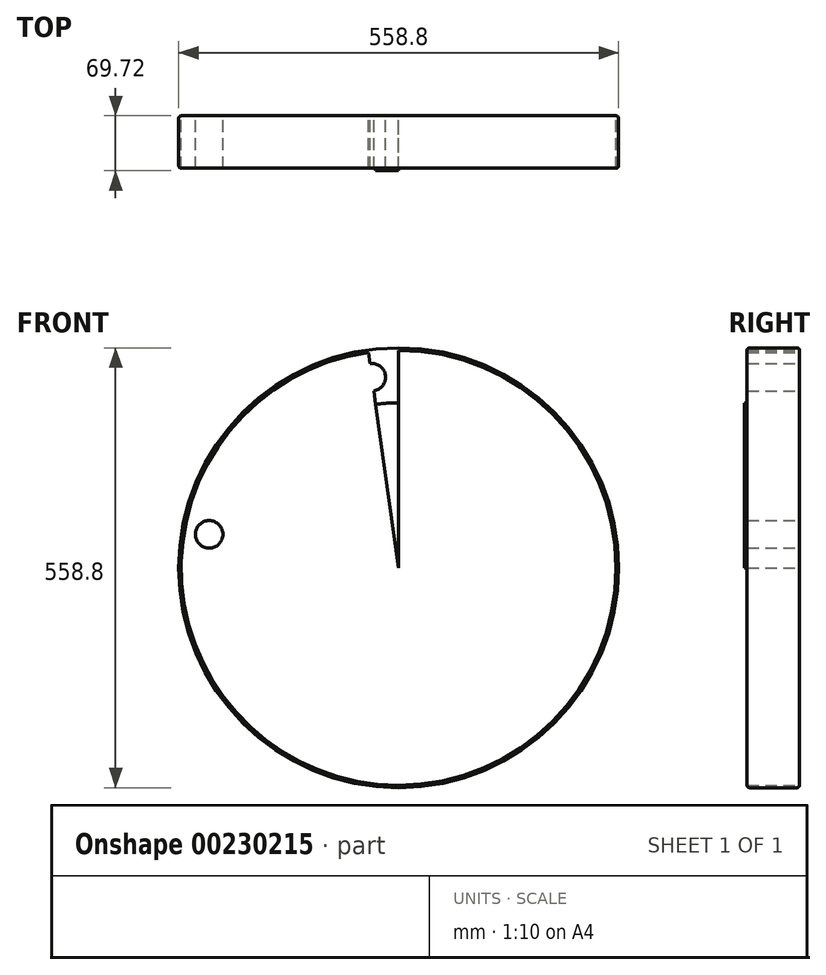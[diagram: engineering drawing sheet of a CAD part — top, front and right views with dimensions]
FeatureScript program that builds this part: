
annotation { "Feature Type Name" : "Feature", "Feature Type Description" : "" }
export const myFeature = defineFeature(function(context is Context, id is Id, definition is map)
    precondition{}
    {
        {
            var Q0;
            Q0=qCreatedBy(makeId("Front.planeOp"),FACE);
            var sketch = newSketch(context, id + "F0", { "sketchPlane" : qUnion([Q0])});
            skCircle(sketch, "E0", {"center": v(0, 0) * mm, "radius": 279.4 * mm});
            skSolve(sketch);
        }
        {
            var Q0;
            Q0 = qSketchRegion(id + "F0", true);
            extrude(context, id + "F1", {"entities" : qUnion([Q0]), "depth" : 66.55 * mm});
        }
        {
            var Q0;
            Q0=makeQuery(id+"F1.opExtrude","CAP_EDGE",EDGE,{"disambiguationData":[OSD([sQuery(id+"F0.wireOp",EDGE,"E0")])],"isStart":false});
            var Q1;
            Q1=makeQuery(id+"F1.opExtrude","CAP_EDGE",EDGE,{"disambiguationData":[OSD([sQuery(id+"F0.wireOp",EDGE,"E0")])],"isStart":true});
            fillet(context, id + "F2", {"entities" : qUnion([Q0, Q1]), "radius" : 3.17 * mm, "tangentPropagation" : true, "allowEdgeOverflow" : false});
        }
        {
            var Q0;
            Q0=makeQuery(id+"F1.opExtrude","CAP_FACE",FACE,{"disambiguationData":[OSD([sQuery(id+"F0.wireOp",EDGE,"E0")])],"isStart":false});
            var sketch = newSketch(context, id + "F3", { "sketchPlane" : qUnion([Q0])});
            skCircle(sketch, "E1", {"center": v(0, 0) * mm, "radius": 209.55 * mm});
            skSolve(sketch);
        }
        {
            var Q0;
            Q0 = qSketchRegion(id + "F3", true);
            extrude(context, id + "F4", {"entities" : qUnion([Q0]), "operationType" : NewBodyOperationType.ADD, "depth" : 3.17 * mm});
        }
        {
            var Q0;
            Q0=makeQuery(id+"F1.opExtrude","CAP_FACE",FACE,{"disambiguationData":[OSD([sQuery(id+"F0.wireOp",EDGE,"E0")])],"isStart":true});
            var sketch = newSketch(context, id + "F5", { "sketchPlane" : qUnion([Q0])});
            skCircle(sketch, "E2", {"center": v(0, 0) * mm, "radius": 244.48 * mm});
            skLineSegment(sketch, "E3", {"start": v(0, 0) * mm, "end": v(0, 323.68) * mm});
            skLineSegment(sketch, "E4", {"start": v(0, 0) * mm, "end": v(45.3, 322.28) * mm});
            skCircle(sketch, "E5", {"center": v(34.02, 242.1) * mm, "radius": 17.46 * mm});
            skCircle(sketch, "E6.1.0", {"center": v(-42.45, 240.76) * mm, "radius": 17.46 * mm});
            skCircle(sketch, "E6.2.0", {"center": v(-114.77, 215.86) * mm, "radius": 17.46 * mm});
            skCircle(sketch, "E6.3.0", {"center": v(-175.86, 169.83) * mm, "radius": 17.46 * mm});
            skCircle(sketch, "E6.4.0", {"center": v(-219.73, 107.17) * mm, "radius": 17.46 * mm});
            skCircle(sketch, "E6.5.0", {"center": v(-242.1, 34.02) * mm, "radius": 17.46 * mm});
            skCircle(sketch, "E6.6.0", {"center": v(-240.76, -42.45) * mm, "radius": 17.46 * mm});
            skCircle(sketch, "E6.7.0", {"center": v(-215.86, -114.77) * mm, "radius": 17.46 * mm});
            skCircle(sketch, "E6.8.0", {"center": v(-169.83, -175.86) * mm, "radius": 17.46 * mm});
            skCircle(sketch, "E6.9.0", {"center": v(-107.17, -219.73) * mm, "radius": 17.46 * mm});
            skCircle(sketch, "E6.10.0", {"center": v(-34.02, -242.1) * mm, "radius": 17.46 * mm});
            skCircle(sketch, "E6.11.0", {"center": v(42.45, -240.76) * mm, "radius": 17.46 * mm});
            skCircle(sketch, "E6.12.0", {"center": v(114.77, -215.86) * mm, "radius": 17.46 * mm});
            skCircle(sketch, "E6.13.0", {"center": v(175.86, -169.83) * mm, "radius": 17.46 * mm});
            skCircle(sketch, "E6.14.0", {"center": v(219.73, -107.17) * mm, "radius": 17.46 * mm});
            skCircle(sketch, "E6.15.0", {"center": v(242.1, -34.02) * mm, "radius": 17.46 * mm});
            skCircle(sketch, "E6.16.0", {"center": v(240.76, 42.45) * mm, "radius": 17.46 * mm});
            skCircle(sketch, "E6.17.0", {"center": v(215.86, 114.77) * mm, "radius": 17.46 * mm});
            skCircle(sketch, "E6.18.0", {"center": v(169.83, 175.86) * mm, "radius": 17.46 * mm});
            skCircle(sketch, "E6.19.0", {"center": v(107.17, 219.73) * mm, "radius": 17.46 * mm});
            skSolve(sketch);
        }
        {
            var Q0;
            {var subQ0=sQuery(id+"F5.wireOp",EDGE,"E6.16.0");var subQ1=sQuery(id+"F5.wireOp",EDGE,"E2");var subQ2=makeQuery(id+"F5.imprint","INTERSECT",VERTEX,{"disambiguationData":[OD(0.0)],"derivedFrom":[subQ1,subQ0]});Q0=makeQuery(id+"F5.imprint","IMPRINT",FACE,{"disambiguationData":[TD([[makeQuery(id+"F5.imprint","IMPRINT",EDGE,{"disambiguationData":[TD([[subQ2,1.0]])],"derivedFrom":subQ1}),1.0]])]});}
            var Q1;
            {var subQ0=sQuery(id+"F5.wireOp",EDGE,"E6.16.0");var subQ1=sQuery(id+"F5.wireOp",EDGE,"E2");var subQ2=makeQuery(id+"F5.imprint","INTERSECT",VERTEX,{"disambiguationData":[OD(0.0)],"derivedFrom":[subQ1,subQ0]});Q1=makeQuery(id+"F5.imprint","IMPRINT",FACE,{"disambiguationData":[TD([[makeQuery(id+"F5.imprint","IMPRINT",EDGE,{"disambiguationData":[TD([[subQ2,1.0]])],"derivedFrom":subQ1}),-1.0]])]});}
            var Q2;
            {var subQ0=sQuery(id+"F5.wireOp",EDGE,"E6.17.0");var subQ1=sQuery(id+"F5.wireOp",EDGE,"E2");var subQ2=makeQuery(id+"F5.imprint","INTERSECT",VERTEX,{"disambiguationData":[OD(0.0)],"derivedFrom":[subQ1,subQ0]});Q2=makeQuery(id+"F5.imprint","IMPRINT",FACE,{"disambiguationData":[TD([[makeQuery(id+"F5.imprint","IMPRINT",EDGE,{"disambiguationData":[TD([[subQ2,-1.0]])],"derivedFrom":subQ1}),1.0]])]});}
            var Q3;
            {var subQ0=sQuery(id+"F5.wireOp",EDGE,"E6.17.0");var subQ1=sQuery(id+"F5.wireOp",EDGE,"E2");var subQ2=makeQuery(id+"F5.imprint","INTERSECT",VERTEX,{"disambiguationData":[OD(0.0)],"derivedFrom":[subQ1,subQ0]});Q3=makeQuery(id+"F5.imprint","IMPRINT",FACE,{"disambiguationData":[TD([[makeQuery(id+"F5.imprint","IMPRINT",EDGE,{"disambiguationData":[TD([[subQ2,-1.0]])],"derivedFrom":subQ1}),-1.0]])]});}
            var Q4;
            {var subQ0=sQuery(id+"F5.wireOp",EDGE,"E6.18.0");var subQ1=sQuery(id+"F5.wireOp",EDGE,"E2");var subQ2=makeQuery(id+"F5.imprint","INTERSECT",VERTEX,{"disambiguationData":[OD(0.0)],"derivedFrom":[subQ1,subQ0]});Q4=makeQuery(id+"F5.imprint","IMPRINT",FACE,{"disambiguationData":[TD([[makeQuery(id+"F5.imprint","IMPRINT",EDGE,{"disambiguationData":[TD([[subQ2,-1.0]])],"derivedFrom":subQ1}),1.0]])]});}
            var Q5;
            {var subQ0=sQuery(id+"F5.wireOp",EDGE,"E6.18.0");var subQ1=sQuery(id+"F5.wireOp",EDGE,"E2");var subQ2=makeQuery(id+"F5.imprint","INTERSECT",VERTEX,{"disambiguationData":[OD(0.0)],"derivedFrom":[subQ1,subQ0]});Q5=makeQuery(id+"F5.imprint","IMPRINT",FACE,{"disambiguationData":[TD([[makeQuery(id+"F5.imprint","IMPRINT",EDGE,{"disambiguationData":[TD([[subQ2,-1.0]])],"derivedFrom":subQ1}),-1.0]])]});}
            var Q6;
            {var subQ0=sQuery(id+"F5.wireOp",EDGE,"E6.19.0");var subQ1=sQuery(id+"F5.wireOp",EDGE,"E2");var subQ2=makeQuery(id+"F5.imprint","INTERSECT",VERTEX,{"disambiguationData":[OD(0.0)],"derivedFrom":[subQ1,subQ0]});Q6=makeQuery(id+"F5.imprint","IMPRINT",FACE,{"disambiguationData":[TD([[makeQuery(id+"F5.imprint","IMPRINT",EDGE,{"disambiguationData":[TD([[subQ2,-1.0]])],"derivedFrom":subQ1}),1.0]])]});}
            var Q7;
            {var subQ0=sQuery(id+"F5.wireOp",EDGE,"E6.19.0");var subQ1=sQuery(id+"F5.wireOp",EDGE,"E2");var subQ2=makeQuery(id+"F5.imprint","INTERSECT",VERTEX,{"disambiguationData":[OD(0.0)],"derivedFrom":[subQ1,subQ0]});Q7=makeQuery(id+"F5.imprint","IMPRINT",FACE,{"disambiguationData":[TD([[makeQuery(id+"F5.imprint","IMPRINT",EDGE,{"disambiguationData":[TD([[subQ2,-1.0]])],"derivedFrom":subQ1}),-1.0]])]});}
            var Q8;
            {var subQ0=sQuery(id+"F5.wireOp",EDGE,"E6.1.0");var subQ1=sQuery(id+"F5.wireOp",EDGE,"E2");var subQ2=makeQuery(id+"F5.imprint","INTERSECT",VERTEX,{"disambiguationData":[OD(0.0)],"derivedFrom":[subQ1,subQ0]});Q8=makeQuery(id+"F5.imprint","IMPRINT",FACE,{"disambiguationData":[TD([[makeQuery(id+"F5.imprint","IMPRINT",EDGE,{"disambiguationData":[TD([[subQ2,-1.0]])],"derivedFrom":subQ1}),1.0]])]});}
            var Q9;
            {var subQ0=sQuery(id+"F5.wireOp",EDGE,"E6.1.0");var subQ1=sQuery(id+"F5.wireOp",EDGE,"E2");var subQ2=makeQuery(id+"F5.imprint","INTERSECT",VERTEX,{"disambiguationData":[OD(0.0)],"derivedFrom":[subQ1,subQ0]});Q9=makeQuery(id+"F5.imprint","IMPRINT",FACE,{"disambiguationData":[TD([[makeQuery(id+"F5.imprint","IMPRINT",EDGE,{"disambiguationData":[TD([[subQ2,-1.0]])],"derivedFrom":subQ1}),-1.0]])]});}
            var Q10;
            {var subQ0=sQuery(id+"F5.wireOp",EDGE,"E6.2.0");var subQ1=sQuery(id+"F5.wireOp",EDGE,"E2");var subQ2=makeQuery(id+"F5.imprint","INTERSECT",VERTEX,{"disambiguationData":[OD(0.0)],"derivedFrom":[subQ1,subQ0]});Q10=makeQuery(id+"F5.imprint","IMPRINT",FACE,{"disambiguationData":[TD([[makeQuery(id+"F5.imprint","IMPRINT",EDGE,{"disambiguationData":[TD([[subQ2,-1.0]])],"derivedFrom":subQ1}),1.0]])]});}
            var Q11;
            {var subQ0=sQuery(id+"F5.wireOp",EDGE,"E6.2.0");var subQ1=sQuery(id+"F5.wireOp",EDGE,"E2");var subQ2=makeQuery(id+"F5.imprint","INTERSECT",VERTEX,{"disambiguationData":[OD(0.0)],"derivedFrom":[subQ1,subQ0]});Q11=makeQuery(id+"F5.imprint","IMPRINT",FACE,{"disambiguationData":[TD([[makeQuery(id+"F5.imprint","IMPRINT",EDGE,{"disambiguationData":[TD([[subQ2,-1.0]])],"derivedFrom":subQ1}),-1.0]])]});}
            var Q12;
            {var subQ0=sQuery(id+"F5.wireOp",EDGE,"E6.3.0");var subQ1=sQuery(id+"F5.wireOp",EDGE,"E2");var subQ2=makeQuery(id+"F5.imprint","INTERSECT",VERTEX,{"disambiguationData":[OD(0.0)],"derivedFrom":[subQ1,subQ0]});Q12=makeQuery(id+"F5.imprint","IMPRINT",FACE,{"disambiguationData":[TD([[makeQuery(id+"F5.imprint","IMPRINT",EDGE,{"disambiguationData":[TD([[subQ2,-1.0]])],"derivedFrom":subQ1}),1.0]])]});}
            var Q13;
            {var subQ0=sQuery(id+"F5.wireOp",EDGE,"E6.3.0");var subQ1=sQuery(id+"F5.wireOp",EDGE,"E2");var subQ2=makeQuery(id+"F5.imprint","INTERSECT",VERTEX,{"disambiguationData":[OD(0.0)],"derivedFrom":[subQ1,subQ0]});Q13=makeQuery(id+"F5.imprint","IMPRINT",FACE,{"disambiguationData":[TD([[makeQuery(id+"F5.imprint","IMPRINT",EDGE,{"disambiguationData":[TD([[subQ2,-1.0]])],"derivedFrom":subQ1}),-1.0]])]});}
            var Q14;
            {var subQ0=sQuery(id+"F5.wireOp",EDGE,"E6.4.0");var subQ1=sQuery(id+"F5.wireOp",EDGE,"E2");var subQ2=makeQuery(id+"F5.imprint","INTERSECT",VERTEX,{"disambiguationData":[OD(0.0)],"derivedFrom":[subQ1,subQ0]});Q14=makeQuery(id+"F5.imprint","IMPRINT",FACE,{"disambiguationData":[TD([[makeQuery(id+"F5.imprint","IMPRINT",EDGE,{"disambiguationData":[TD([[subQ2,-1.0]])],"derivedFrom":subQ1}),1.0]])]});}
            var Q15;
            {var subQ0=sQuery(id+"F5.wireOp",EDGE,"E6.4.0");var subQ1=sQuery(id+"F5.wireOp",EDGE,"E2");var subQ2=makeQuery(id+"F5.imprint","INTERSECT",VERTEX,{"disambiguationData":[OD(0.0)],"derivedFrom":[subQ1,subQ0]});Q15=makeQuery(id+"F5.imprint","IMPRINT",FACE,{"disambiguationData":[TD([[makeQuery(id+"F5.imprint","IMPRINT",EDGE,{"disambiguationData":[TD([[subQ2,-1.0]])],"derivedFrom":subQ1}),-1.0]])]});}
            var Q16;
            {var subQ0=sQuery(id+"F5.wireOp",EDGE,"E6.5.0");var subQ1=sQuery(id+"F5.wireOp",EDGE,"E2");var subQ2=makeQuery(id+"F5.imprint","INTERSECT",VERTEX,{"disambiguationData":[OD(0.0)],"derivedFrom":[subQ1,subQ0]});Q16=makeQuery(id+"F5.imprint","IMPRINT",FACE,{"disambiguationData":[TD([[makeQuery(id+"F5.imprint","IMPRINT",EDGE,{"disambiguationData":[TD([[subQ2,-1.0]])],"derivedFrom":subQ1}),1.0]])]});}
            var Q17;
            {var subQ0=sQuery(id+"F5.wireOp",EDGE,"E6.5.0");var subQ1=sQuery(id+"F5.wireOp",EDGE,"E2");var subQ2=makeQuery(id+"F5.imprint","INTERSECT",VERTEX,{"disambiguationData":[OD(0.0)],"derivedFrom":[subQ1,subQ0]});Q17=makeQuery(id+"F5.imprint","IMPRINT",FACE,{"disambiguationData":[TD([[makeQuery(id+"F5.imprint","IMPRINT",EDGE,{"disambiguationData":[TD([[subQ2,-1.0]])],"derivedFrom":subQ1}),-1.0]])]});}
            var Q18;
            {var subQ0=sQuery(id+"F5.wireOp",EDGE,"E6.6.0");var subQ1=sQuery(id+"F5.wireOp",EDGE,"E2");var subQ2=makeQuery(id+"F5.imprint","INTERSECT",VERTEX,{"disambiguationData":[OD(0.0)],"derivedFrom":[subQ1,subQ0]});Q18=makeQuery(id+"F5.imprint","IMPRINT",FACE,{"disambiguationData":[TD([[makeQuery(id+"F5.imprint","IMPRINT",EDGE,{"disambiguationData":[TD([[subQ2,-1.0]])],"derivedFrom":subQ1}),1.0]])]});}
            var Q19;
            {var subQ0=sQuery(id+"F5.wireOp",EDGE,"E6.6.0");var subQ1=sQuery(id+"F5.wireOp",EDGE,"E2");var subQ2=makeQuery(id+"F5.imprint","INTERSECT",VERTEX,{"disambiguationData":[OD(0.0)],"derivedFrom":[subQ1,subQ0]});Q19=makeQuery(id+"F5.imprint","IMPRINT",FACE,{"disambiguationData":[TD([[makeQuery(id+"F5.imprint","IMPRINT",EDGE,{"disambiguationData":[TD([[subQ2,-1.0]])],"derivedFrom":subQ1}),-1.0]])]});}
            var Q20;
            {var subQ0=sQuery(id+"F5.wireOp",EDGE,"E6.7.0");var subQ1=sQuery(id+"F5.wireOp",EDGE,"E2");var subQ2=makeQuery(id+"F5.imprint","INTERSECT",VERTEX,{"disambiguationData":[OD(0.0)],"derivedFrom":[subQ1,subQ0]});Q20=makeQuery(id+"F5.imprint","IMPRINT",FACE,{"disambiguationData":[TD([[makeQuery(id+"F5.imprint","IMPRINT",EDGE,{"disambiguationData":[TD([[subQ2,-1.0]])],"derivedFrom":subQ1}),1.0]])]});}
            var Q21;
            {var subQ0=sQuery(id+"F5.wireOp",EDGE,"E6.7.0");var subQ1=sQuery(id+"F5.wireOp",EDGE,"E2");var subQ2=makeQuery(id+"F5.imprint","INTERSECT",VERTEX,{"disambiguationData":[OD(0.0)],"derivedFrom":[subQ1,subQ0]});Q21=makeQuery(id+"F5.imprint","IMPRINT",FACE,{"disambiguationData":[TD([[makeQuery(id+"F5.imprint","IMPRINT",EDGE,{"disambiguationData":[TD([[subQ2,-1.0]])],"derivedFrom":subQ1}),-1.0]])]});}
            var Q22;
            {var subQ0=sQuery(id+"F5.wireOp",EDGE,"E6.8.0");var subQ1=sQuery(id+"F5.wireOp",EDGE,"E2");var subQ2=makeQuery(id+"F5.imprint","INTERSECT",VERTEX,{"disambiguationData":[OD(0.0)],"derivedFrom":[subQ1,subQ0]});Q22=makeQuery(id+"F5.imprint","IMPRINT",FACE,{"disambiguationData":[TD([[makeQuery(id+"F5.imprint","IMPRINT",EDGE,{"disambiguationData":[TD([[subQ2,-1.0]])],"derivedFrom":subQ1}),1.0]])]});}
            var Q23;
            {var subQ0=sQuery(id+"F5.wireOp",EDGE,"E6.8.0");var subQ1=sQuery(id+"F5.wireOp",EDGE,"E2");var subQ2=makeQuery(id+"F5.imprint","INTERSECT",VERTEX,{"disambiguationData":[OD(0.0)],"derivedFrom":[subQ1,subQ0]});Q23=makeQuery(id+"F5.imprint","IMPRINT",FACE,{"disambiguationData":[TD([[makeQuery(id+"F5.imprint","IMPRINT",EDGE,{"disambiguationData":[TD([[subQ2,-1.0]])],"derivedFrom":subQ1}),-1.0]])]});}
            var Q24;
            {var subQ0=sQuery(id+"F5.wireOp",EDGE,"E6.9.0");var subQ1=sQuery(id+"F5.wireOp",EDGE,"E2");var subQ2=makeQuery(id+"F5.imprint","INTERSECT",VERTEX,{"disambiguationData":[OD(0.0)],"derivedFrom":[subQ1,subQ0]});Q24=makeQuery(id+"F5.imprint","IMPRINT",FACE,{"disambiguationData":[TD([[makeQuery(id+"F5.imprint","IMPRINT",EDGE,{"disambiguationData":[TD([[subQ2,-1.0]])],"derivedFrom":subQ1}),1.0]])]});}
            var Q25;
            {var subQ0=sQuery(id+"F5.wireOp",EDGE,"E6.9.0");var subQ1=sQuery(id+"F5.wireOp",EDGE,"E2");var subQ2=makeQuery(id+"F5.imprint","INTERSECT",VERTEX,{"disambiguationData":[OD(0.0)],"derivedFrom":[subQ1,subQ0]});Q25=makeQuery(id+"F5.imprint","IMPRINT",FACE,{"disambiguationData":[TD([[makeQuery(id+"F5.imprint","IMPRINT",EDGE,{"disambiguationData":[TD([[subQ2,-1.0]])],"derivedFrom":subQ1}),-1.0]])]});}
            var Q26;
            {var subQ0=sQuery(id+"F5.wireOp",EDGE,"E6.10.0");var subQ1=sQuery(id+"F5.wireOp",EDGE,"E2");var subQ2=makeQuery(id+"F5.imprint","INTERSECT",VERTEX,{"disambiguationData":[OD(0.0)],"derivedFrom":[subQ1,subQ0]});Q26=makeQuery(id+"F5.imprint","IMPRINT",FACE,{"disambiguationData":[TD([[makeQuery(id+"F5.imprint","IMPRINT",EDGE,{"disambiguationData":[TD([[subQ2,-1.0]])],"derivedFrom":subQ1}),1.0]])]});}
            var Q27;
            {var subQ0=sQuery(id+"F5.wireOp",EDGE,"E6.10.0");var subQ1=sQuery(id+"F5.wireOp",EDGE,"E2");var subQ2=makeQuery(id+"F5.imprint","INTERSECT",VERTEX,{"disambiguationData":[OD(0.0)],"derivedFrom":[subQ1,subQ0]});Q27=makeQuery(id+"F5.imprint","IMPRINT",FACE,{"disambiguationData":[TD([[makeQuery(id+"F5.imprint","IMPRINT",EDGE,{"disambiguationData":[TD([[subQ2,-1.0]])],"derivedFrom":subQ1}),-1.0]])]});}
            var Q28;
            {var subQ0=sQuery(id+"F5.wireOp",EDGE,"E6.11.0");var subQ1=sQuery(id+"F5.wireOp",EDGE,"E2");var subQ2=makeQuery(id+"F5.imprint","INTERSECT",VERTEX,{"disambiguationData":[OD(0.0)],"derivedFrom":[subQ1,subQ0]});Q28=makeQuery(id+"F5.imprint","IMPRINT",FACE,{"disambiguationData":[TD([[makeQuery(id+"F5.imprint","IMPRINT",EDGE,{"disambiguationData":[TD([[subQ2,-1.0]])],"derivedFrom":subQ1}),1.0]])]});}
            var Q29;
            {var subQ0=sQuery(id+"F5.wireOp",EDGE,"E6.11.0");var subQ1=sQuery(id+"F5.wireOp",EDGE,"E2");var subQ2=makeQuery(id+"F5.imprint","INTERSECT",VERTEX,{"disambiguationData":[OD(0.0)],"derivedFrom":[subQ1,subQ0]});Q29=makeQuery(id+"F5.imprint","IMPRINT",FACE,{"disambiguationData":[TD([[makeQuery(id+"F5.imprint","IMPRINT",EDGE,{"disambiguationData":[TD([[subQ2,-1.0]])],"derivedFrom":subQ1}),-1.0]])]});}
            var Q30;
            {var subQ0=sQuery(id+"F5.wireOp",EDGE,"E6.12.0");var subQ1=sQuery(id+"F5.wireOp",EDGE,"E2");var subQ2=makeQuery(id+"F5.imprint","INTERSECT",VERTEX,{"disambiguationData":[OD(0.0)],"derivedFrom":[subQ1,subQ0]});Q30=makeQuery(id+"F5.imprint","IMPRINT",FACE,{"disambiguationData":[TD([[makeQuery(id+"F5.imprint","IMPRINT",EDGE,{"disambiguationData":[TD([[subQ2,-1.0]])],"derivedFrom":subQ1}),1.0]])]});}
            var Q31;
            {var subQ0=sQuery(id+"F5.wireOp",EDGE,"E6.12.0");var subQ1=sQuery(id+"F5.wireOp",EDGE,"E2");var subQ2=makeQuery(id+"F5.imprint","INTERSECT",VERTEX,{"disambiguationData":[OD(0.0)],"derivedFrom":[subQ1,subQ0]});Q31=makeQuery(id+"F5.imprint","IMPRINT",FACE,{"disambiguationData":[TD([[makeQuery(id+"F5.imprint","IMPRINT",EDGE,{"disambiguationData":[TD([[subQ2,-1.0]])],"derivedFrom":subQ1}),-1.0]])]});}
            var Q32;
            {var subQ0=sQuery(id+"F5.wireOp",EDGE,"E6.13.0");var subQ1=sQuery(id+"F5.wireOp",EDGE,"E2");var subQ2=makeQuery(id+"F5.imprint","INTERSECT",VERTEX,{"disambiguationData":[OD(0.0)],"derivedFrom":[subQ1,subQ0]});Q32=makeQuery(id+"F5.imprint","IMPRINT",FACE,{"disambiguationData":[TD([[makeQuery(id+"F5.imprint","IMPRINT",EDGE,{"disambiguationData":[TD([[subQ2,-1.0]])],"derivedFrom":subQ1}),1.0]])]});}
            var Q33;
            {var subQ0=sQuery(id+"F5.wireOp",EDGE,"E6.13.0");var subQ1=sQuery(id+"F5.wireOp",EDGE,"E2");var subQ2=makeQuery(id+"F5.imprint","INTERSECT",VERTEX,{"disambiguationData":[OD(0.0)],"derivedFrom":[subQ1,subQ0]});Q33=makeQuery(id+"F5.imprint","IMPRINT",FACE,{"disambiguationData":[TD([[makeQuery(id+"F5.imprint","IMPRINT",EDGE,{"disambiguationData":[TD([[subQ2,-1.0]])],"derivedFrom":subQ1}),-1.0]])]});}
            var Q34;
            {var subQ0=sQuery(id+"F5.wireOp",EDGE,"E6.14.0");var subQ1=sQuery(id+"F5.wireOp",EDGE,"E2");var subQ2=makeQuery(id+"F5.imprint","INTERSECT",VERTEX,{"disambiguationData":[OD(0.0)],"derivedFrom":[subQ1,subQ0]});Q34=makeQuery(id+"F5.imprint","IMPRINT",FACE,{"disambiguationData":[TD([[makeQuery(id+"F5.imprint","IMPRINT",EDGE,{"disambiguationData":[TD([[subQ2,-1.0]])],"derivedFrom":subQ1}),1.0]])]});}
            var Q35;
            {var subQ0=sQuery(id+"F5.wireOp",EDGE,"E6.14.0");var subQ1=sQuery(id+"F5.wireOp",EDGE,"E2");var subQ2=makeQuery(id+"F5.imprint","INTERSECT",VERTEX,{"disambiguationData":[OD(0.0)],"derivedFrom":[subQ1,subQ0]});Q35=makeQuery(id+"F5.imprint","IMPRINT",FACE,{"disambiguationData":[TD([[makeQuery(id+"F5.imprint","IMPRINT",EDGE,{"disambiguationData":[TD([[subQ2,-1.0]])],"derivedFrom":subQ1}),-1.0]])]});}
            var Q36;
            {var subQ0=sQuery(id+"F5.wireOp",EDGE,"E6.15.0");var subQ1=sQuery(id+"F5.wireOp",EDGE,"E2");var subQ2=makeQuery(id+"F5.imprint","INTERSECT",VERTEX,{"disambiguationData":[OD(0.0)],"derivedFrom":[subQ1,subQ0]});Q36=makeQuery(id+"F5.imprint","IMPRINT",FACE,{"disambiguationData":[TD([[makeQuery(id+"F5.imprint","IMPRINT",EDGE,{"disambiguationData":[TD([[subQ2,-1.0]])],"derivedFrom":subQ1}),1.0]])]});}
            var Q37;
            {var subQ0=sQuery(id+"F5.wireOp",EDGE,"E6.15.0");var subQ1=sQuery(id+"F5.wireOp",EDGE,"E2");var subQ2=makeQuery(id+"F5.imprint","INTERSECT",VERTEX,{"disambiguationData":[OD(0.0)],"derivedFrom":[subQ1,subQ0]});Q37=makeQuery(id+"F5.imprint","IMPRINT",FACE,{"disambiguationData":[TD([[makeQuery(id+"F5.imprint","IMPRINT",EDGE,{"disambiguationData":[TD([[subQ2,-1.0]])],"derivedFrom":subQ1}),-1.0]])]});}
            var Q38;
            {var subQ0=sQuery(id+"F5.wireOp",EDGE,"E5");var subQ1=sQuery(id+"F5.wireOp",EDGE,"E2");var subQ2=makeQuery(id+"F5.imprint","INTERSECT",VERTEX,{"disambiguationData":[OD(0.0)],"derivedFrom":[subQ1,subQ0]});Q38=makeQuery(id+"F5.imprint","IMPRINT",FACE,{"disambiguationData":[TD([[makeQuery(id+"F5.imprint","IMPRINT",EDGE,{"disambiguationData":[TD([[subQ2,-1.0]])],"derivedFrom":subQ1}),1.0]])]});}
            var Q39;
            {var subQ0=sQuery(id+"F5.wireOp",EDGE,"E5");var subQ1=sQuery(id+"F5.wireOp",EDGE,"E2");var subQ2=makeQuery(id+"F5.imprint","INTERSECT",VERTEX,{"disambiguationData":[OD(0.0)],"derivedFrom":[subQ1,subQ0]});Q39=makeQuery(id+"F5.imprint","IMPRINT",FACE,{"disambiguationData":[TD([[makeQuery(id+"F5.imprint","IMPRINT",EDGE,{"disambiguationData":[TD([[subQ2,-1.0]])],"derivedFrom":subQ1}),-1.0]])]});}
            var Q40;
            {var subQ0=sQuery(id+"F5.wireOp",EDGE,"E4");var subQ1=sQuery(id+"F5.wireOp",EDGE,"E2");var subQ2=makeQuery(id+"F5.imprint","INTERSECT",VERTEX,{"derivedFrom":[subQ1,subQ0]});Q40=makeQuery(id+"F5.imprint","IMPRINT",FACE,{"disambiguationData":[TD([[makeQuery(id+"F5.imprint","IMPRINT",EDGE,{"disambiguationData":[TD([[subQ2,-1.0]])],"derivedFrom":subQ1}),1.0]])]});}
            var Q41;
            {var subQ0=sQuery(id+"F5.wireOp",EDGE,"E4");var subQ1=sQuery(id+"F5.wireOp",EDGE,"E2");var subQ2=makeQuery(id+"F5.imprint","INTERSECT",VERTEX,{"derivedFrom":[subQ1,subQ0]});Q41=makeQuery(id+"F5.imprint","IMPRINT",FACE,{"disambiguationData":[TD([[makeQuery(id+"F5.imprint","IMPRINT",EDGE,{"disambiguationData":[TD([[subQ2,-1.0]])],"derivedFrom":subQ1}),-1.0]])]});}
            extrude(context, id + "F6", {"entities" : qUnion([Q0, Q1, Q2, Q3, Q4, Q5, Q6, Q7, Q8, Q9, Q10, Q11, Q12, Q13, Q14, Q15, Q16, Q17, Q18, Q19, Q20, Q21, Q22, Q23, Q24, Q25, Q26, Q27, Q28, Q29, Q30, Q31, Q32, Q33, Q34, Q35, Q36, Q37, Q38, Q39, Q40, Q41]), "operationType" : NewBodyOperationType.REMOVE, "oppositeDirection" : true, "depth" : 76.2 * mm});
        }
    });
